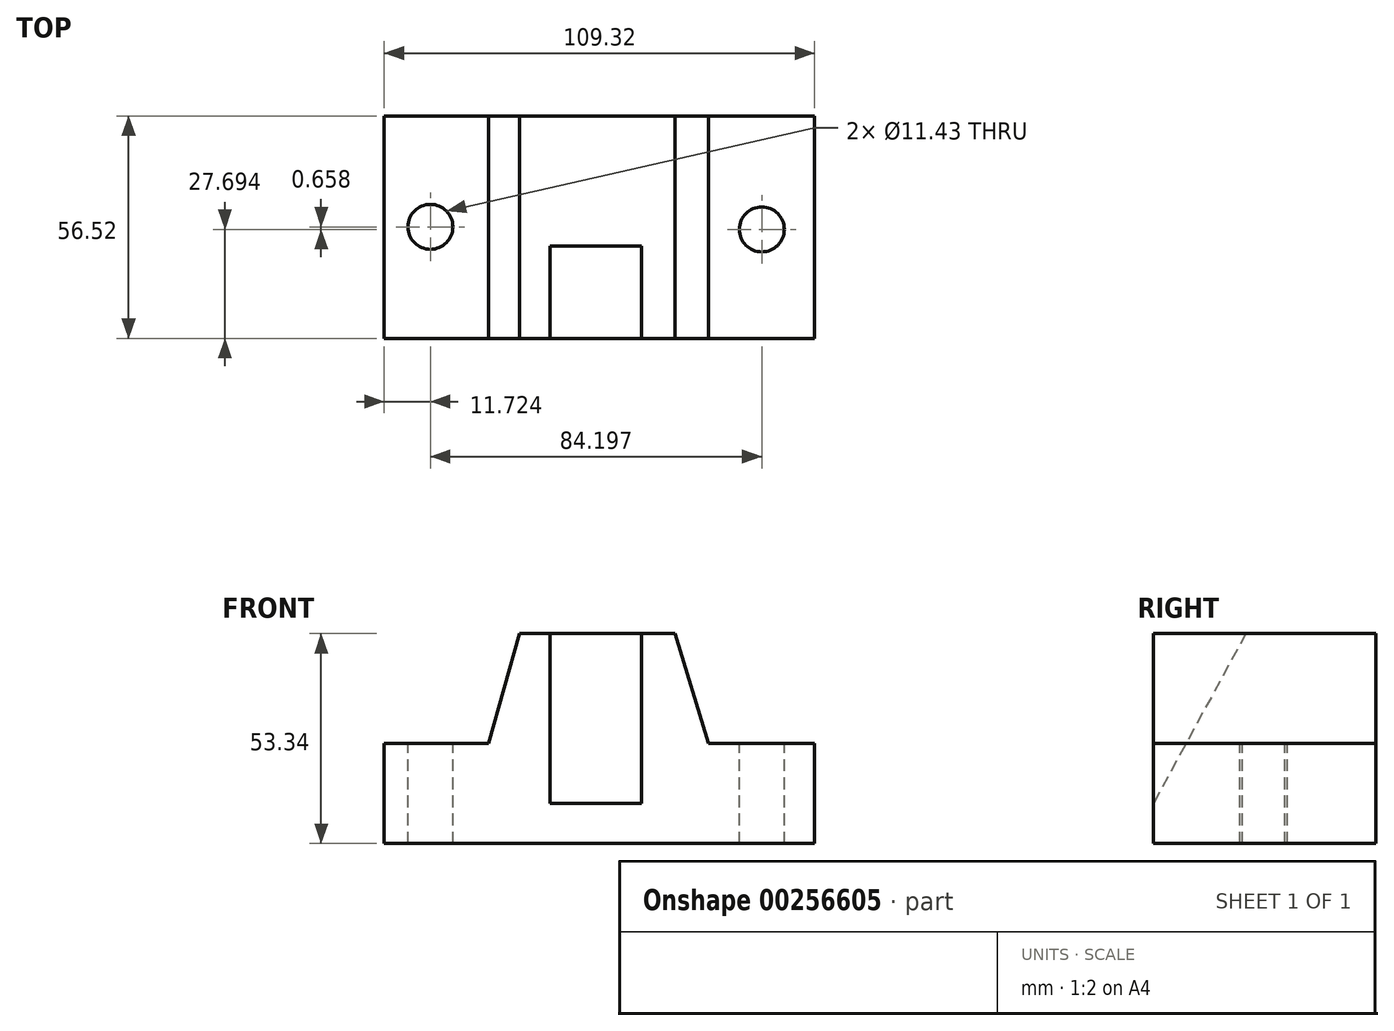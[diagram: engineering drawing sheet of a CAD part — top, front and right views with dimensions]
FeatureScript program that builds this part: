
annotation { "Feature Type Name" : "Feature", "Feature Type Description" : "" }
export const myFeature = defineFeature(function(context is Context, id is Id, definition is map)
    precondition{}
    {
        {
            var Q0;
            Q0=qCreatedBy(makeId("Top.planeOp"),FACE);
            var sketch = newSketch(context, id + "F0", { "sketchPlane" : qUnion([Q0])});
            skLineSegment(sketch, "E0.bottom", {"start": v(-54.3, 33.03) * mm, "end": v(55, 33.03) * mm});
            skLineSegment(sketch, "E0.top", {"start": v(-54.3, -23.5) * mm, "end": v(55, -23.5) * mm});
            skLineSegment(sketch, "E0.left", {"start": v(-54.3, 33.03) * mm, "end": v(-54.3, -23.5) * mm});
            skLineSegment(sketch, "E0.right", {"start": v(55, 33.03) * mm, "end": v(55, -23.5) * mm});
            skSolve(sketch);
        }
        {
            var Q0;
            Q0=makeQuery(id+"F0.imprint","IMPRINT",FACE,{"disambiguationData":[TD([[makeQuery(id+"F0.imprint","IMPRINT",EDGE,{"derivedFrom":sQuery(id+"F0.wireOp",EDGE,"E0.bottom")}),-1.0]])]});
            extrude(context, id + "F1", {"entities" : qUnion([Q0]), "depth" : 25.4 * mm});
        }
        {
            var Q0;
            Q0=makeQuery(id+"F1.opExtrude","CAP_FACE",FACE,{"disambiguationData":[OSD([sQuery(id+"F0.wireOp",EDGE,"E0.bottom"),sQuery(id+"F0.wireOp",EDGE,"E0.top"),sQuery(id+"F0.wireOp",EDGE,"E0.left"),sQuery(id+"F0.wireOp",EDGE,"E0.right")])],"isStart":false});
            var sketch = newSketch(context, id + "F2", { "sketchPlane" : qUnion([Q0])});
            skLineSegment(sketch, "E1.bottom", {"start": v(-27.8, 33.03) * mm, "end": v(28.03, 33.03) * mm});
            skLineSegment(sketch, "E1.top", {"start": v(-27.8, -23.5) * mm, "end": v(28.03, -23.5) * mm});
            skLineSegment(sketch, "E1.left", {"start": v(-27.8, 33.03) * mm, "end": v(-27.8, -23.5) * mm});
            skLineSegment(sketch, "E1.right", {"start": v(28.03, 33.03) * mm, "end": v(28.03, -23.5) * mm});
            skSolve(sketch);
        }
        {
            var Q0;
            Q0=makeQuery(id+"F2.imprint","IMPRINT",FACE,{"disambiguationData":[TD([[makeQuery(id+"F2.imprint","IMPRINT",EDGE,{"derivedFrom":sQuery(id+"F2.wireOp",EDGE,"E1.bottom")}),-1.0]])]});
            extrude(context, id + "F3", {"entities" : qUnion([Q0]), "operationType" : NewBodyOperationType.ADD, "depth" : 27.94 * mm});
        }
        {
            var Q0;
            Q0=makeQuery(id+"F3.opExtrude","CAP_FACE",FACE,{"disambiguationData":[OSD([sQuery(id+"F2.wireOp",EDGE,"E1.bottom"),sQuery(id+"F2.wireOp",EDGE,"E1.top"),sQuery(id+"F2.wireOp",EDGE,"E1.left"),sQuery(id+"F2.wireOp",EDGE,"E1.right")])],"isStart":false});
            var sketch = newSketch(context, id + "F4", { "sketchPlane" : qUnion([Q0])});
            skLineSegment(sketch, "E2.bottom", {"start": v(-12.21, 0) * mm, "end": v(11.05, 0) * mm});
            skLineSegment(sketch, "E2.top", {"start": v(-12.21, -23.5) * mm, "end": v(11.05, -23.5) * mm});
            skLineSegment(sketch, "E2.left", {"start": v(-12.21, 0) * mm, "end": v(-12.21, -23.5) * mm});
            skLineSegment(sketch, "E2.right", {"start": v(11.05, 0) * mm, "end": v(11.05, -23.5) * mm});
            skSolve(sketch);
        }
        {
            var Q0;
            Q0=makeQuery(id+"F4.imprint","IMPRINT",FACE,{"disambiguationData":[TD([[makeQuery(id+"F4.imprint","IMPRINT",EDGE,{"derivedFrom":sQuery(id+"F4.wireOp",EDGE,"E2.bottom")}),-1.0]])]});
            extrude(context, id + "F5", {"entities" : qUnion([Q0]), "operationType" : NewBodyOperationType.REMOVE, "oppositeDirection" : true, "depth" : 43.18 * mm});
        }
        {
            var Q0;
            Q0=makeQuery(id+"F3.boolean.opBoolean","MERGE",FACE,{"derivedFrom":[makeQuery(id+"F1.opExtrude","SWEPT_FACE",FACE,{"disambiguationData":[OSD([sQuery(id+"F0.wireOp",EDGE,"E0.top")])]}),makeQuery(id+"F3.opExtrude","SWEPT_FACE",FACE,{"disambiguationData":[OSD([sQuery(id+"F2.wireOp",EDGE,"E1.top")])]})]});
            var sketch = newSketch(context, id + "F6", { "sketchPlane" : qUnion([Q0])});
            skLineSegment(sketch, "E3", {"start": v(-20, 53.34) * mm, "end": v(-27.8, 25.4) * mm});
            skSolve(sketch);
        }
        {
            var Q0;
            {var subQ0=sQuery(id+"F6.wireOp",EDGE,"E3");Q0=makeQuery(id+"F6.imprint","IMPRINT",FACE,{"disambiguationData":[TD([[makeQuery(id+"F6.imprint","IMPRINT",EDGE,{"derivedFrom":subQ0}),-1.0]])]});}
            extrude(context, id + "F7", {"entities" : qUnion([Q0]), "operationType" : NewBodyOperationType.REMOVE, "oppositeDirection" : true, "depth" : 25.4 * mm});
        }
        {
            var Q0;
            Q0=makeQuery(id+"F7.boolean.opBoolean","COPY",FACE,{"derivedFrom":makeQuery(id+"F7.opExtrude","CAP_FACE",FACE,{"disambiguationData":[OSD([sQuery(id+"F0.wireOp",EDGE,"E0.top"),sQuery(id+"F2.wireOp",EDGE,"E1.top"),sQuery(id+"F2.wireOp",EDGE,"E1.left"),sQuery(id+"F6.wireOp",EDGE,"E3")])],"isStart":false})});
            extrude(context, id + "F8", {"entities" : qUnion([Q0]), "operationType" : NewBodyOperationType.REMOVE, "oppositeDirection" : true, "depth" : 38.1 * mm});
        }
        {
            var Q0;
            Q0=makeQuery(id+"F3.boolean.opBoolean","MERGE",FACE,{"derivedFrom":[makeQuery(id+"F1.opExtrude","SWEPT_FACE",FACE,{"disambiguationData":[OSD([sQuery(id+"F0.wireOp",EDGE,"E0.top")])]}),makeQuery(id+"F3.opExtrude","SWEPT_FACE",FACE,{"disambiguationData":[OSD([sQuery(id+"F2.wireOp",EDGE,"E1.top")])]})]});
            var sketch = newSketch(context, id + "F9", { "sketchPlane" : qUnion([Q0])});
            skLineSegment(sketch, "E4", {"start": v(19.54, 53.34) * mm, "end": v(28.03, 25.4) * mm});
            skSolve(sketch);
        }
        {
            var Q0;
            {var subQ0=sQuery(id+"F9.wireOp",EDGE,"E4");Q0=makeQuery(id+"F9.imprint","IMPRINT",FACE,{"disambiguationData":[TD([[makeQuery(id+"F9.imprint","IMPRINT",EDGE,{"derivedFrom":subQ0}),1.0]])]});}
            extrude(context, id + "F10", {"entities" : qUnion([Q0]), "operationType" : NewBodyOperationType.REMOVE, "oppositeDirection" : true, "depth" : 58.42 * mm});
        }
        {
            var Q0;
            Q0=makeQuery(id+"F5.boolean.opBoolean","COPY",FACE,{"derivedFrom":makeQuery(id+"F5.opExtrude","SWEPT_FACE",FACE,{"disambiguationData":[OSD([sQuery(id+"F4.wireOp",EDGE,"E2.left")])]})});
            var sketch = newSketch(context, id + "F11", { "sketchPlane" : qUnion([Q0])});
            skLineSegment(sketch, "E5", {"start": v(0, 53.34) * mm, "end": v(-23.5, 10.16) * mm});
            skSolve(sketch);
        }
        {
            var Q0;
            Q0=makeQuery(id+"F11.imprint","IMPRINT",FACE,{"disambiguationData":[TD([[makeQuery(id+"F11.imprint","IMPRINT",EDGE,{"derivedFrom":sQuery(id+"F11.wireOp",EDGE,"E5")}),1.0]])]});
            extrude(context, id + "F12", {"entities" : qUnion([Q0]), "operationType" : NewBodyOperationType.ADD, "depth" : 25.4 * mm});
        }
        {
            var Q0;
            {var subQ0=sQuery(id+"F0.wireOp",EDGE,"E0.left");var subQ1=sQuery(id+"F0.wireOp",EDGE,"E0.top");var subQ2=sQuery(id+"F0.wireOp",EDGE,"E0.bottom");Q0=makeQuery(id+"F3.boolean.opBoolean","SPLIT",FACE,{"disambiguationData":[TD([makeQuery(id+"F1.opExtrude","SWEPT_FACE",FACE,{"disambiguationData":[OSD([subQ0])]})])],"derivedFrom":makeQuery(id+"F1.opExtrude","CAP_FACE",FACE,{"disambiguationData":[OSD([subQ2,subQ1,subQ0,sQuery(id+"F0.wireOp",EDGE,"E0.right")])],"isStart":false})});}
            var sketch = newSketch(context, id + "F13", { "sketchPlane" : qUnion([Q0])});
            skCircle(sketch, "E6", {"center": v(-42.59, 4.86) * mm, "radius": 5.71 * mm});
            skSolve(sketch);
        }
        {
            var Q0;
            Q0=sQuery(id+"F13.wireOp",VERTEX,"E6.center");
            var Q1;
            Q1=makeQuery(id+"F1.opExtrude","SWEPT_BODY",BODY,{"disambiguationData":[OSD([sQuery(id+"F0.wireOp",EDGE,"E0.bottom"),sQuery(id+"F0.wireOp",EDGE,"E0.top"),sQuery(id+"F0.wireOp",EDGE,"E0.left"),sQuery(id+"F0.wireOp",EDGE,"E0.right")])]});
            hole(context, id + "F14", {"style" : HoleStyle.SIMPLE, "endStyle" : HoleEndStyle.THROUGH, "holeDiameter" : 11.43 * mm, "tappedDepth" : 12.7 * mm, "tapClearance" : 3, "locations" : qUnion([Q0]), "scope" : qUnion([Q1])});
        }
        {
            var Q0;
            {var subQ0=sQuery(id+"F0.wireOp",EDGE,"E0.right");var subQ1=sQuery(id+"F0.wireOp",EDGE,"E0.top");var subQ2=sQuery(id+"F0.wireOp",EDGE,"E0.bottom");Q0=makeQuery(id+"F3.boolean.opBoolean","SPLIT",FACE,{"disambiguationData":[TD([makeQuery(id+"F1.opExtrude","SWEPT_FACE",FACE,{"disambiguationData":[OSD([subQ0])]})])],"derivedFrom":makeQuery(id+"F1.opExtrude","CAP_FACE",FACE,{"disambiguationData":[OSD([subQ2,subQ1,sQuery(id+"F0.wireOp",EDGE,"E0.left"),subQ0])],"isStart":false})});}
            var sketch = newSketch(context, id + "F15", { "sketchPlane" : qUnion([Q0])});
            skCircle(sketch, "E7", {"center": v(41.61, 4.2) * mm, "radius": 6.25 * mm});
            skSolve(sketch);
        }
        {
            var Q0;
            Q0=sQuery(id+"F15.wireOp",VERTEX,"E7.center");
            var Q1;
            Q1=makeQuery(id+"F1.opExtrude","SWEPT_BODY",BODY,{"disambiguationData":[OSD([sQuery(id+"F0.wireOp",EDGE,"E0.bottom"),sQuery(id+"F0.wireOp",EDGE,"E0.top"),sQuery(id+"F0.wireOp",EDGE,"E0.left"),sQuery(id+"F0.wireOp",EDGE,"E0.right")])]});
            hole(context, id + "F16", {"style" : HoleStyle.SIMPLE, "endStyle" : HoleEndStyle.THROUGH, "holeDiameter" : 11.43 * mm, "tappedDepth" : 12.7 * mm, "tapClearance" : 3, "locations" : qUnion([Q0]), "scope" : qUnion([Q1])});
        }
    });
